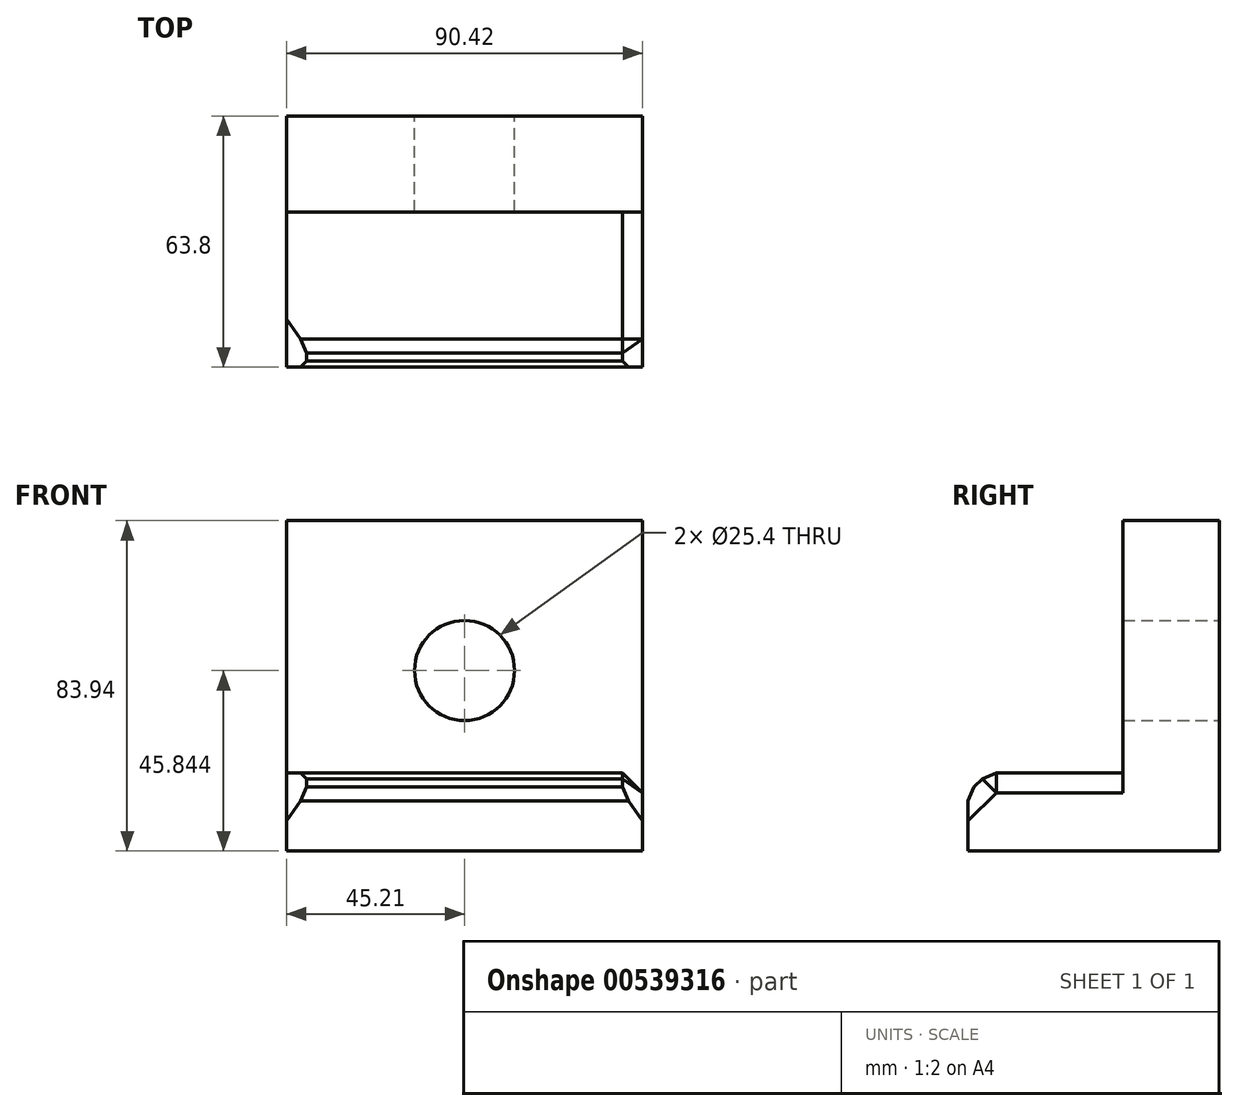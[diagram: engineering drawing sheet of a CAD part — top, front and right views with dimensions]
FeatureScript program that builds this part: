
annotation { "Feature Type Name" : "Feature", "Feature Type Description" : "" }
export const myFeature = defineFeature(function(context is Context, id is Id, definition is map)
    precondition{}
    {
        {
            var Q0;
            Q0=qCreatedBy(makeId("Right.planeOp"),FACE);
            var sketch = newSketch(context, id + "F0", { "sketchPlane" : qUnion([Q0])});
            skLineSegment(sketch, "E0", {"start": v(24.42, 44.87) * mm, "end": v(24.42, -39.07) * mm});
            skLineSegment(sketch, "E1", {"start": v(24.42, -39.07) * mm, "end": v(-39.38, -39.07) * mm});
            skLineSegment(sketch, "E2", {"start": v(-39.38, -39.07) * mm, "end": v(-39.38, -19.23) * mm});
            skLineSegment(sketch, "E3", {"start": v(-39.38, -19.23) * mm, "end": v(0, -19.23) * mm});
            skLineSegment(sketch, "E4", {"start": v(24.42, 44.87) * mm, "end": v(0, 44.87) * mm});
            skLineSegment(sketch, "E5", {"start": v(0, 44.87) * mm, "end": v(0, -19.23) * mm});
            skSolve(sketch);
        }
        {
            var Q0;
            Q0=makeQuery(id+"F0.imprint","IMPRINT",FACE,{"disambiguationData":[TD([[makeQuery(id+"F0.imprint","IMPRINT",EDGE,{"derivedFrom":sQuery(id+"F0.wireOp",EDGE,"E0")}),-1.0]])]});
            extrude(context, id + "F1", {"entities" : qUnion([Q0]), "endBound" : BoundingType.SYMMETRIC, "depth" : 90.42 * mm, "offsetDistance" : 25.4 * mm});
        }
        {
            var Q0;
            Q0=makeQuery(id+"F1.opExtrude","SWEPT_FACE",FACE,{"disambiguationData":[OSD([sQuery(id+"F0.wireOp",EDGE,"E0")])]});
            var sketch = newSketch(context, id + "F2", { "sketchPlane" : qUnion([Q0])});
            skCircle(sketch, "E6", {"center": v(0, 6.77) * mm, "radius": 12.7 * mm});
            skSolve(sketch);
        }
        {
            var Q0;
            Q0=makeQuery(id+"F2.imprint","IMPRINT",FACE,{"disambiguationData":[TD([[makeQuery(id+"F2.imprint","IMPRINT",EDGE,{"derivedFrom":sQuery(id+"F2.wireOp",EDGE,"E6")}),1.0]])]});
            extrude(context, id + "F3", {"entities" : qUnion([Q0]), "operationType" : NewBodyOperationType.REMOVE, "oppositeDirection" : true, "depth" : 25.4 * mm, "offsetDistance" : 25.4 * mm});
        }
        {
            var Q0;
            Q0=makeQuery(id+"F1.opExtrude","SWEPT_EDGE",EDGE,{"disambiguationData":[OSD([sQuery(id+"F0.wireOp",EDGE,"E2"),sQuery(id+"F0.wireOp",EDGE,"E3")])]});
            chamfer(context, id + "F4", {"entities" : qUnion([Q0]), "width" : 5.08 * mm});
        }
        {
            var Q0;
            Q0=makeQuery(id+"F4.opChamfer","BLEND_FACE",FACE,{"disambiguationData":[OSD([sQuery(id+"F0.wireOp",EDGE,"E2"),sQuery(id+"F0.wireOp",EDGE,"E3")])]});
            var Q1;
            {var subQ0=sQuery(id+"F0.wireOp",EDGE,"E3");Q1=makeQuery(id+"F4.opChamfer","BLEND_EDGE",EDGE,{"blendedFrom":[makeQuery(id+"F1.opExtrude","SWEPT_EDGE",EDGE,{"disambiguationData":[OSD([sQuery(id+"F0.wireOp",EDGE,"E2"),subQ0])]}),makeQuery(id+"F1.opExtrude","SWEPT_FACE",FACE,{"disambiguationData":[OSD([subQ0])]})],"blendedInto":[makeQuery(id+"F1.opExtrude","SWEPT_FACE",FACE,{"disambiguationData":[OSD([subQ0])]})]});}
            var Q2;
            Q2=makeQuery(id+"F1.opExtrude","CAP_EDGE",EDGE,{"disambiguationData":[OSD([sQuery(id+"F0.wireOp",EDGE,"E3")])],"isStart":false});
            chamfer(context, id + "F5", {"entities" : qUnion([Q0, Q1, Q2]), "width" : 5.08 * mm});
        }
    });
